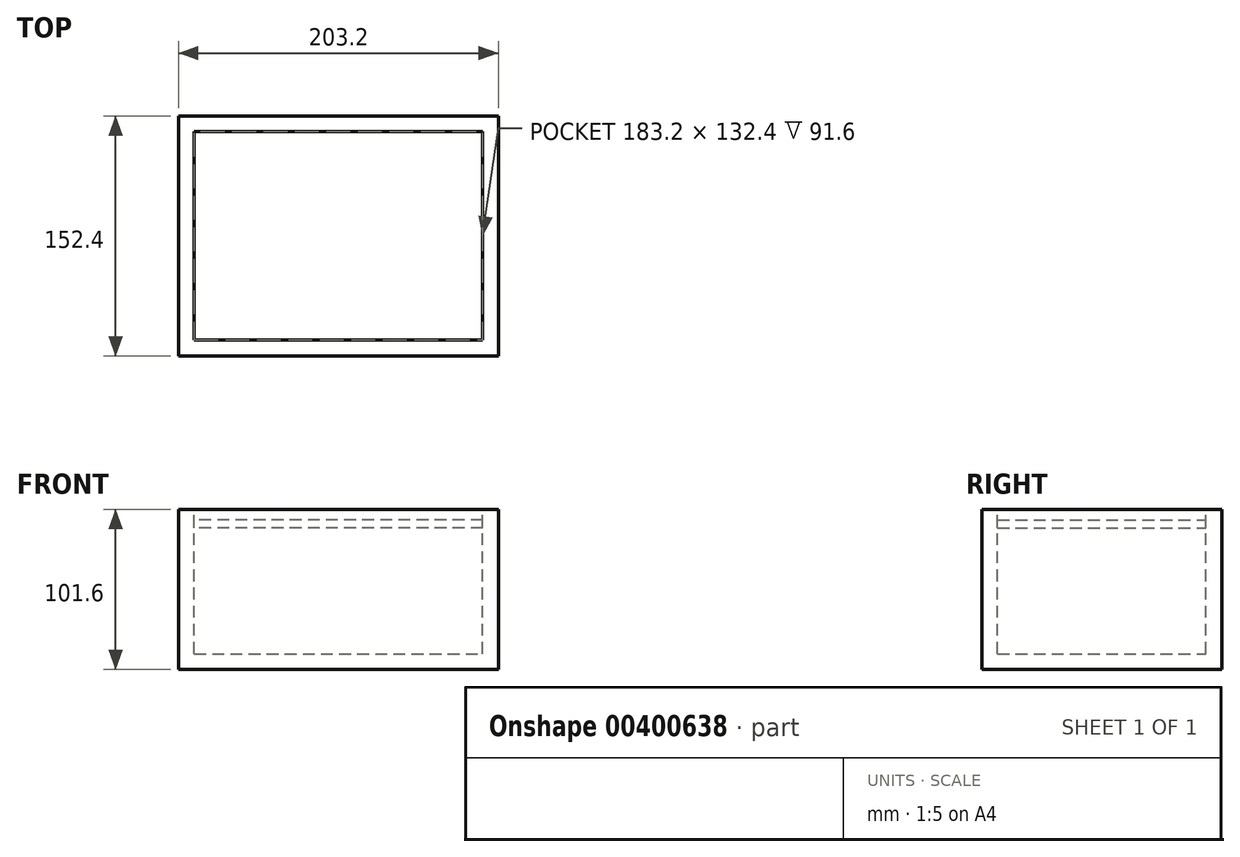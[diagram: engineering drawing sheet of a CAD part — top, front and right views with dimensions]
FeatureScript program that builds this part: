
annotation { "Feature Type Name" : "Feature", "Feature Type Description" : "" }
export const myFeature = defineFeature(function(context is Context, id is Id, definition is map)
    precondition{}
    {
        {
            var Q0;
            Q0=qCreatedBy(makeId("Front.planeOp"),FACE);
            var sketch = newSketch(context, id + "F0", { "sketchPlane" : qUnion([Q0])});
            skLineSegment(sketch, "E0.bottom", {"start": v(-101.6, -50.8) * mm, "end": v(101.6, -50.8) * mm});
            skLineSegment(sketch, "E0.top", {"start": v(-101.6, 50.8) * mm, "end": v(101.6, 50.8) * mm});
            skLineSegment(sketch, "E0.left", {"start": v(-101.6, -50.8) * mm, "end": v(-101.6, 50.8) * mm});
            skLineSegment(sketch, "E0.right", {"start": v(101.6, -50.8) * mm, "end": v(101.6, 50.8) * mm});
            skPoint(sketch, "E0.middle", {"position": v(0, 0) * mm});
            skSolve(sketch);
        }
        {
            var Q0;
            Q0 = qSketchRegion(id + "F0", true);
            extrude(context, id + "F1", {"entities" : qUnion([Q0]), "depth" : 152.4 * mm, "symmetric" : true});
        }
        {
            var Q0;
            Q0=makeQuery(id+"F1.opExtrude","SWEPT_FACE",FACE,{"disambiguationData":[OSD([sQuery(id+"F0.wireOp",EDGE,"E0.top")])]});
            shell(context, id + "F2", {"entities" : qUnion([Q0]), "thickness" : 10 * mm});
        }
        {
            var Q0;
            Q0=makeQuery(id+"F2.opShell","OFFSET_FACE",FACE,{"disambiguationData":[OSD([sQuery(id+"F0.wireOp",EDGE,"E0.left")])]});
            var sketch = newSketch(context, id + "F3", { "sketchPlane" : qUnion([Q0])});
            skLineSegment(sketch, "E1.bottom", {"start": v(-66.2, 44.19) * mm, "end": v(66.2, 44.19) * mm});
            skLineSegment(sketch, "E1.top", {"start": v(-66.2, 39.1) * mm, "end": v(66.2, 39.1) * mm});
            skLineSegment(sketch, "E1.left", {"start": v(-66.2, 44.19) * mm, "end": v(-66.2, 39.1) * mm});
            skLineSegment(sketch, "E1.right", {"start": v(66.2, 44.19) * mm, "end": v(66.2, 39.1) * mm});
            skSolve(sketch);
        }
        {
            var Q0;
            Q0=makeQuery(id+"F3.imprint","IMPRINT",FACE,{"disambiguationData":[TD([[makeQuery(id+"F3.imprint","IMPRINT",EDGE,{"derivedFrom":sQuery(id+"F3.wireOp",EDGE,"E1.bottom")}),-1.0]])]});
            extrude(context, id + "F4", {"entities" : qUnion([Q0]), "depth" : 183.2 * mm});
        }
    });
